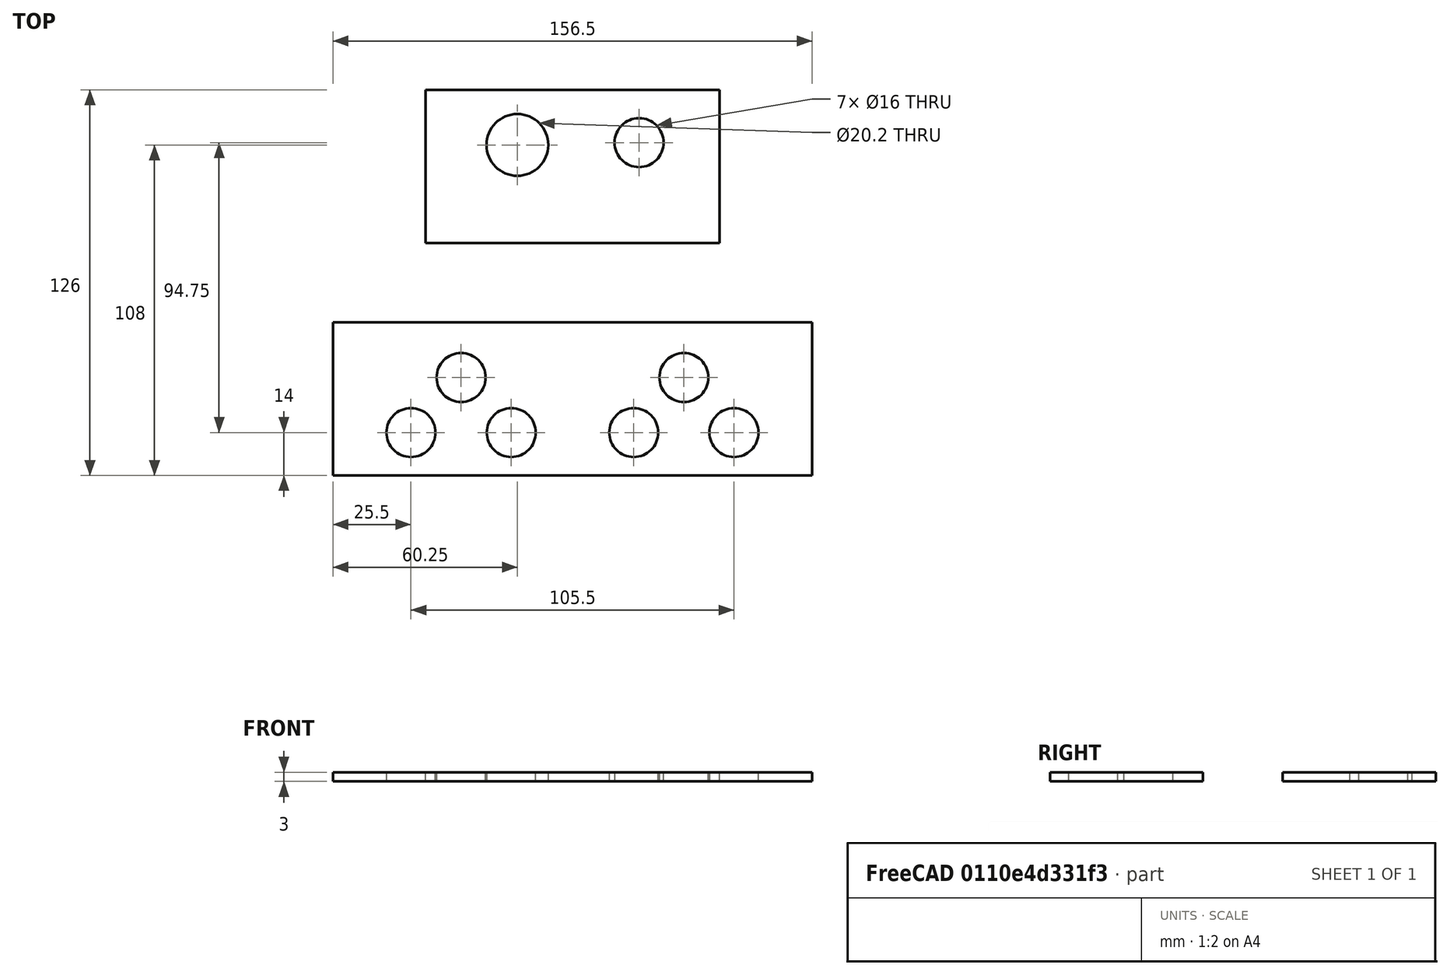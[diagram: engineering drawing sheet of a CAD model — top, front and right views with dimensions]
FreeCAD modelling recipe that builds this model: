
FCSTD DOCUMENT  (FreeCAD 0.21R33771 (Git))
Label: relay-enclosure
License: All rights reserved
LicenseURL: http://en.wikipedia.org/wiki/All_rights_reserved
objects: TechDraw::DrawViewDimension×7, Sketcher::SketchObject×2, PartDesign::Pad×2, PartDesign::Body×2, TechDraw::DrawViewPart×2, TechDraw::DrawSVGTemplate×1, TechDraw::DrawPage×1
note: 15 computed .brp shape members not serialized (recipe doc carries the construction recipe); baked Part::Feature solids carry a one-line shape summary decoded from their .brp

FEATURE [Sketcher::SketchObject] Sketch
  FullyConstrained = true
  MapMode = 5
  Support = -> [XY_Plane]
  sketch-geometry (32):
    g0: LineSegment StartX=-78.25 StartY=-25 StartZ=0 EndX=78.25 EndY=-25 EndZ=0
    g1: LineSegment StartX=78.25 StartY=-25 StartZ=0 EndX=78.25 EndY=25 EndZ=0
    g2: LineSegment StartX=78.25 StartY=25 StartZ=0 EndX=-78.25 EndY=25 EndZ=0
    g3: LineSegment StartX=-78.25 StartY=25 StartZ=0 EndX=-78.25 EndY=-25 EndZ=0
    g4: Circle CenterX=-52.75 CenterY=-11 CenterZ=0 NormalX=0 NormalY=0 NormalZ=1 AngleXU=0 Radius=8
    g5: Circle CenterX=-36.375 CenterY=7 CenterZ=0 NormalX=0 NormalY=0 NormalZ=1 AngleXU=0 Radius=8
    g6: Circle CenterX=0 CenterY=7 CenterZ=0 NormalX=0 NormalY=0 NormalZ=1 AngleXU=0 Radius=10.1
    g7: Circle CenterX=20 CenterY=-11 CenterZ=0 NormalX=0 NormalY=0 NormalZ=1 AngleXU=0 Radius=8
    g8: Circle CenterX=-20 CenterY=-11 CenterZ=0 NormalX=0 NormalY=0 NormalZ=1 AngleXU=0 Radius=8
    g9: Circle CenterX=52.75 CenterY=-11 CenterZ=0 NormalX=0 NormalY=0 NormalZ=1 AngleXU=0 Radius=8
    g10: Circle CenterX=36.375 CenterY=7 CenterZ=0 NormalX=0 NormalY=0 NormalZ=1 AngleXU=0 Radius=8
    g11: LineSegment StartX=75.25 StartY=25 StartZ=0 EndX=75.25 EndY=-23 EndZ=0
    g12: LineSegment StartX=75.25 StartY=-23 StartZ=0 EndX=-75.25 EndY=-23 EndZ=0
    g13: LineSegment StartX=-75.25 StartY=-23 StartZ=0 EndX=-75.25 EndY=25 EndZ=0
    g14: Circle CenterX=-52.75 CenterY=-11 CenterZ=0 NormalX=0 NormalY=0 NormalZ=1 AngleXU=0 Radius=10.75
    g15: Circle CenterX=-36.375 CenterY=7 CenterZ=0 NormalX=0 NormalY=0 NormalZ=1 AngleXU=0 Radius=10.75
    g16: Circle CenterX=20 CenterY=-11 CenterZ=0 NormalX=0 NormalY=0 NormalZ=1 AngleXU=0 Radius=10.75
    g17: Circle CenterX=0 CenterY=7 CenterZ=0 NormalX=0 NormalY=0 NormalZ=1 AngleXU=0 Radius=15
    g18: Circle CenterX=-20 CenterY=-11 CenterZ=0 NormalX=0 NormalY=0 NormalZ=1 AngleXU=0 Radius=10.75
    g19: Circle CenterX=52.75 CenterY=-11 CenterZ=0 NormalX=0 NormalY=0 NormalZ=1 AngleXU=0 Radius=10.75
    g20: Circle CenterX=36.375 CenterY=7 CenterZ=0 NormalX=0 NormalY=0 NormalZ=1 AngleXU=0 Radius=10.75
    g21: GeomPoint X=75.25 Y=1 Z=0
    g22: GeomPoint X=-75.25 Y=1 Z=0
    g23: LineSegment StartX=-75.25 StartY=1 StartZ=0 EndX=75.25 EndY=1 EndZ=0
    g24: LineSegment StartX=-65 StartY=25 StartZ=0 EndX=-65 EndY=-23 EndZ=0
    g25: LineSegment StartX=65 StartY=-23 StartZ=0 EndX=65 EndY=25 EndZ=0
    g26: LineSegment StartX=-52.75 StartY=1 StartZ=0 EndX=-52.75 EndY=-11 EndZ=0
    g27: LineSegment StartX=-52.75 StartY=-11 StartZ=0 EndX=-52.75 EndY=-23 EndZ=0
    g28: GeomPoint X=-63.5 Y=-11 Z=0
    g29: GeomPoint X=0 Y=22 Z=0
    g30: LineSegment StartX=-52.75 StartY=-11 StartZ=0 EndX=-36.375 EndY=7 EndZ=0
    g31: LineSegment StartX=-36.375 StartY=7 StartZ=0 EndX=-20 EndY=-11 EndZ=0
  constraints (77):
    c: Coincident(g0,g1)
    c: Coincident(g1,g2)
    c: Coincident(g2,g3)
    c: Coincident(g3,g0)
    c: Horizontal(g0)
    c: Horizontal(g2)
    c: Vertical(g1)
    c: Vertical(g3)
    c: Symmetric(g0,g1,g-1)
    c: Diameter(g4) = 16
    c: Equal(g4,g5)
    c: Equal(g7,g4)
    c: Equal(g8,g4)
    c: Equal(g4,g9)
    c: Equal(g10,g4)
    c: Distance(g0) = 156.5
    c: Coincident(g11,g12)
    c: Coincident(g12,g13)
    c: Horizontal(g12)
    c: Vertical(g11)
    c: Vertical(g13)
    c: Distance(g12) = 150.5
    c: Symmetric(g13,g11,g-2)
    c: Distance(g3) = 50
    c: PointOnObject(g13,g2)
    c: Distance(g13) = 48
    c: Coincident(g14,g4)
    c: Diameter(g14) = 21.5
    c: Coincident(g15,g5)
    c: Coincident(g16,g7)
    c: Coincident(g17,g6)
    c: Coincident(g18,g8)
    c: Coincident(g19,g9)
    c: Coincident(g20,g10)
    c: Equal(g14,g15)
    c: Equal(g16,g14)
    c: Equal(g18,g14)
    c: Equal(g20,g14)
    c: Equal(g19,g14)
    c: Symmetric(g11,g11,g21)
    c: Symmetric(g12,g13,g22)
    c: Coincident(g23,g22)
    c: Coincident(g23,g21)
    c: Symmetric(g9,g4,g-2)
    c: Horizontal(g7,g4)
    c: Symmetric(g8,g7,g-2)
    c: PointOnObject(g6,g-2)
    c: Symmetric(g5,g10,g-2)
    c: Horizontal(g5,g6)
    c: PointOnObject(g24,g2)
    c: Vertical(g24)
    c: PointOnObject(g25,g12)
    c: Symmetric(g25,g24,g-2)
    c: Vertical(g25)
    c: PointOnObject(g24,g12)
    c: DistanceX(g24,g25) = 130
    c: PointOnObject(g26,g23)
    c: Coincident(g26,g4)
    c: Coincident(g27,g4)
    c: PointOnObject(g27,g12)
    c: Vertical(g26)
    c: Vertical(g27)
    c: Equal(g26,g27)
    c: Diameter(g6) = 20.2
    c: Diameter(g17) = 30
    c: PointOnObject(g28,g14)
    c: Horizontal(g28,g4)
    c: DistanceX(g24,g28) = 1.5
    c: Vertical(g29,g6)
    c: PointOnObject(g29,g17)
    c: Distance(g29,g2) = 3
    c: DistanceX(g-2,g7) = 20
    c: Coincident(g30,g4)
    c: Coincident(g30,g5)
    c: Coincident(g31,g5)
    c: Coincident(g31,g8)
    c: Equal(g30,g31)
FEATURE [PartDesign::Pad] Pad
  Direction = (0,0,1)
  Length = 3
  Length2 = 10
  Profile = -> Sketch
  ReferenceAxis = -> Sketch [N_Axis]
  Type = 0
FEATURE [PartDesign::Body] Body  label="Front"
  Group = -> [Sketch,Pad]
  Origin = -> Origin
  Tip = -> Pad
FEATURE [Sketcher::SketchObject] Sketch001
  FullyConstrained = true
  MapMode = 5
  Support = -> [XY_Plane001]
  sketch-geometry (17):
    g0: LineSegment StartX=-48 StartY=-25 StartZ=0 EndX=48 EndY=-25 EndZ=0
    g1: LineSegment StartX=48 StartY=-25 StartZ=0 EndX=48 EndY=25 EndZ=0
    g2: LineSegment StartX=48 StartY=25 StartZ=0 EndX=-48 EndY=25 EndZ=0
    g3: LineSegment StartX=-48 StartY=25 StartZ=0 EndX=-48 EndY=-25 EndZ=0
    g4: LineSegment StartX=45 StartY=25 StartZ=0 EndX=45 EndY=-23 EndZ=0
    g5: LineSegment StartX=45 StartY=-23 StartZ=0 EndX=-45 EndY=-23 EndZ=0
    g6: LineSegment StartX=-45 StartY=-23 StartZ=0 EndX=-45 EndY=25 EndZ=0
    g7: LineSegment StartX=-34.5 StartY=25 StartZ=0 EndX=-34.5 EndY=-23 EndZ=0
    g8: LineSegment StartX=34.5 StartY=-23 StartZ=0 EndX=34.5 EndY=25 EndZ=0
    g9: Circle CenterX=-18 CenterY=7 CenterZ=0 NormalX=0 NormalY=0 NormalZ=1 AngleXU=0 Radius=15
    g10: Circle CenterX=-18 CenterY=7 CenterZ=0 NormalX=0 NormalY=0 NormalZ=1 AngleXU=0 Radius=10.1
    g11: Circle CenterX=21.75 CenterY=7.75 CenterZ=0 NormalX=0 NormalY=0 NormalZ=1 AngleXU=0 Radius=8
    g12: Circle CenterX=21.75 CenterY=7.75 CenterZ=0 NormalX=0 NormalY=0 NormalZ=1 AngleXU=0 Radius=12.25
    g13: GeomPoint X=-18 Y=22 Z=0
    g14: GeomPoint X=-33 Y=7 Z=0
    g15: GeomPoint X=34 Y=7.75 Z=0
    g16: GeomPoint X=21.75 Y=20 Z=0
  constraints (45):
    c: Coincident(g0,g1)
    c: Coincident(g1,g2)
    c: Coincident(g2,g3)
    c: Coincident(g3,g0)
    c: Horizontal(g0)
    c: Horizontal(g2)
    c: Vertical(g1)
    c: Vertical(g3)
    c: Symmetric(g0,g1,g-1)
    c: Distance(g0) = 96
    c: Distance(g3) = 50
    c: Coincident(g4,g5)
    c: Coincident(g5,g6)
    c: Horizontal(g5)
    c: Vertical(g4)
    c: Vertical(g6)
    c: PointOnObject(g6,g2)
    c: Symmetric(g6,g4,g-2)
    c: Distance(g6) = 48
    c: PointOnObject(g7,g2)
    c: Vertical(g7)
    c: Vertical(g8)
    c: Symmetric(g7,g8,g-2)
    c: PointOnObject(g7,g5)
    c: PointOnObject(g8,g5)
    c: DistanceX(g7,g8) = 69
    c: Coincident(g10,g9)
    c: Diameter(g10) = 20.2
    c: Diameter(g9) = 30
    c: Coincident(g12,g11)
    c: Diameter(g11) = 16
    c: Diameter(g12) = 24.5
    c: PointOnObject(g13,g9)
    c: Vertical(g13,g10)
    c: Distance(g13,g2) = 3
    c: PointOnObject(g14,g9)
    c: Horizontal(g14,g10)
    c: Distance(g14,g7) = 1.5
    c: PointOnObject(g15,g12)
    c: Horizontal(g15,g11)
    c: Distance(g15,g8) = 0.5
    c: PointOnObject(g16,g12)
    c: Vertical(g16,g11)
    c: Distance(g16,g2) = 5
    c: Distance(g5) = 90
FEATURE [PartDesign::Pad] Pad001
  Direction = (0,0,1)
  Length = 3
  Length2 = 10
  Profile = -> Sketch001
  ReferenceAxis = -> Sketch001 [N_Axis]
  Type = 0
FEATURE [PartDesign::Body] Body001  label="Right"
  Group = -> [Sketch001,Pad001]
  Origin = -> Origin001
  Placement = pos=(0,76,0) rot=(0,0,1;0rad)
  Tip = -> Pad001
FEATURE [TechDraw::DrawSVGTemplate] Template
  EditableTexts = AUTHOR_NAME=Ondřej Sluka; DN=DN; DRAWING_TITLE=CNC relay enclosure; FC-DATE=DD/MM/YYYY; FC-REV=REV A; FC-SC=1:1; FC-SH=X / Y; FC-SI=A4; FreeCAD_DRAWING=FreeCAD DRAWING; PN=PN
  Height = 297
  Orientation = 0
  Template = /app/share/Mod/TechDraw/Templates/A4_Portrait_ISO7200TD.svg
  Width = 210
FEATURE [TechDraw::DrawViewPart] View
  CoarseView = false
  Direction = (0,0,1)
  Focus = 100
  HardHidden = false
  IsoCount = 0
  IsoHidden = false
  IsoVisible = false
  LockPosition = false
  Perspective = false
  Rotation = 0
  ScaleType = 0
  ScrubCount = 0
  SeamHidden = false
  SeamVisible = false
  SmoothHidden = false
  SmoothVisible = true
  Source = -> [Body]
  X = 157.652
  XDirection = (0,-1,0)
  Y = 196.464
FEATURE [TechDraw::DrawViewDimension] Dimension
  AngleOverride = false
  Arbitrary = false
  ArbitraryTolerances = false
  EqualTolerance = true
  ExtensionAngle = 0
  FormatSpec = %.2w
  FormatSpecOverTolerance = %+.2w
  FormatSpecUnderTolerance = %+.2w
  Inverted = false
  LineAngle = 0
  LockPosition = false
  MeasureType = 1
  OverTolerance = 0
  References2D = -> [View]
  Rotation = 0
  ScaleType = 0
  TheoreticalExact = false
  Type = 0
  UnderTolerance = 0
  X = -34.5653
  Y = 2.67391
FEATURE [TechDraw::DrawViewDimension] Dimension001
  AngleOverride = false
  Arbitrary = false
  ArbitraryTolerances = false
  EqualTolerance = true
  ExtensionAngle = 0
  FormatSpec = %.2w
  FormatSpecOverTolerance = %+.2w
  FormatSpecUnderTolerance = %+.2w
  Inverted = false
  LineAngle = 0
  LockPosition = false
  MeasureType = 1
  OverTolerance = 0
  References2D = -> [View]
  Rotation = 0
  ScaleType = 0
  TheoreticalExact = false
  Type = 0
  UnderTolerance = 0
  X = -0.724643
  Y = -89.0834
FEATURE [TechDraw::DrawViewDimension] Dimension002
  AngleOverride = false
  Arbitrary = false
  ArbitraryTolerances = false
  EqualTolerance = true
  ExtensionAngle = 0
  FormatSpec = ⌀%.2w
  FormatSpecOverTolerance = %+.2w
  FormatSpecUnderTolerance = %+.2w
  Inverted = false
  LineAngle = 0
  LockPosition = false
  MeasureType = 1
  OverTolerance = 0
  References2D = -> [View]
  Rotation = 0
  ScaleType = 0
  TheoreticalExact = false
  Type = 5
  UnderTolerance = 0
  X = 2.27514
  Y = 70.1881
FEATURE [TechDraw::DrawViewPart] View001
  CoarseView = false
  Direction = (0,0,1)
  Focus = 100
  HardHidden = false
  IsoCount = 0
  IsoHidden = false
  IsoVisible = false
  LockPosition = false
  Perspective = false
  Rotation = 90
  ScaleType = 0
  ScrubCount = 0
  SeamHidden = false
  SeamVisible = false
  SmoothHidden = false
  SmoothVisible = true
  Source = -> [Body001]
  X = 64.7392
  XDirection = (0.99957,0,0)
  Y = 171.403
FEATURE [TechDraw::DrawViewDimension] Dimension003
  AngleOverride = false
  Arbitrary = false
  ArbitraryTolerances = false
  EqualTolerance = true
  ExtensionAngle = 0
  FormatSpec = %.2w
  FormatSpecOverTolerance = %+.2w
  FormatSpecUnderTolerance = %+.2w
  Inverted = false
  LineAngle = 0
  LockPosition = false
  MeasureType = 1
  OverTolerance = 0
  References2D = -> [View001]
  Rotation = 0
  ScaleType = 0
  TheoreticalExact = false
  Type = 0
  UnderTolerance = 0
  X = -38.0586
  Y = 2.16516
FEATURE [TechDraw::DrawViewDimension] Dimension004
  AngleOverride = false
  Arbitrary = false
  ArbitraryTolerances = false
  EqualTolerance = true
  ExtensionAngle = 0
  FormatSpec = %.2w
  FormatSpecOverTolerance = %+.2w
  FormatSpecUnderTolerance = %+.2w
  Inverted = false
  LineAngle = 0
  LockPosition = false
  MeasureType = 1
  OverTolerance = 0
  References2D = -> [View001]
  Rotation = 0
  ScaleType = 0
  TheoreticalExact = false
  Type = 1
  UnderTolerance = 0
  X = 0.502255
  Y = -62.9115
FEATURE [TechDraw::DrawViewDimension] Dimension005
  AngleOverride = false
  Arbitrary = false
  ArbitraryTolerances = false
  EqualTolerance = true
  ExtensionAngle = 0
  FormatSpec = ⌀%.2w
  FormatSpecOverTolerance = %+.2w
  FormatSpecUnderTolerance = %+.2w
  Inverted = false
  LineAngle = 0
  LockPosition = false
  MeasureType = 1
  OverTolerance = 0
  References2D = -> [View001]
  Rotation = 0
  ScaleType = 0
  TheoreticalExact = false
  Type = 5
  UnderTolerance = 0
  X = 5.35739
  Y = -0.334837
FEATURE [TechDraw::DrawViewDimension] Dimension006
  AngleOverride = false
  Arbitrary = false
  ArbitraryTolerances = false
  EqualTolerance = true
  ExtensionAngle = 0
  FormatSpec = ⌀%.2w
  FormatSpecOverTolerance = %+.2w
  FormatSpecUnderTolerance = %+.2w
  Inverted = false
  LineAngle = 0
  LockPosition = false
  MeasureType = 1
  OverTolerance = 0
  References2D = -> [View001]
  Rotation = 0
  ScaleType = 0
  TheoreticalExact = false
  Type = 5
  UnderTolerance = 0
  X = 6.02706
  Y = 38.6736
FEATURE [TechDraw::DrawPage] Page
  KeepUpdated = true
  NextBalloonIndex = 1
  ProjectionType = 0
  Template = -> Template
  Views = -> [View,Dimension,Dimension001,Dimension002,View001,Dimension003,Dimension004,Dimension005,Dimension006]
